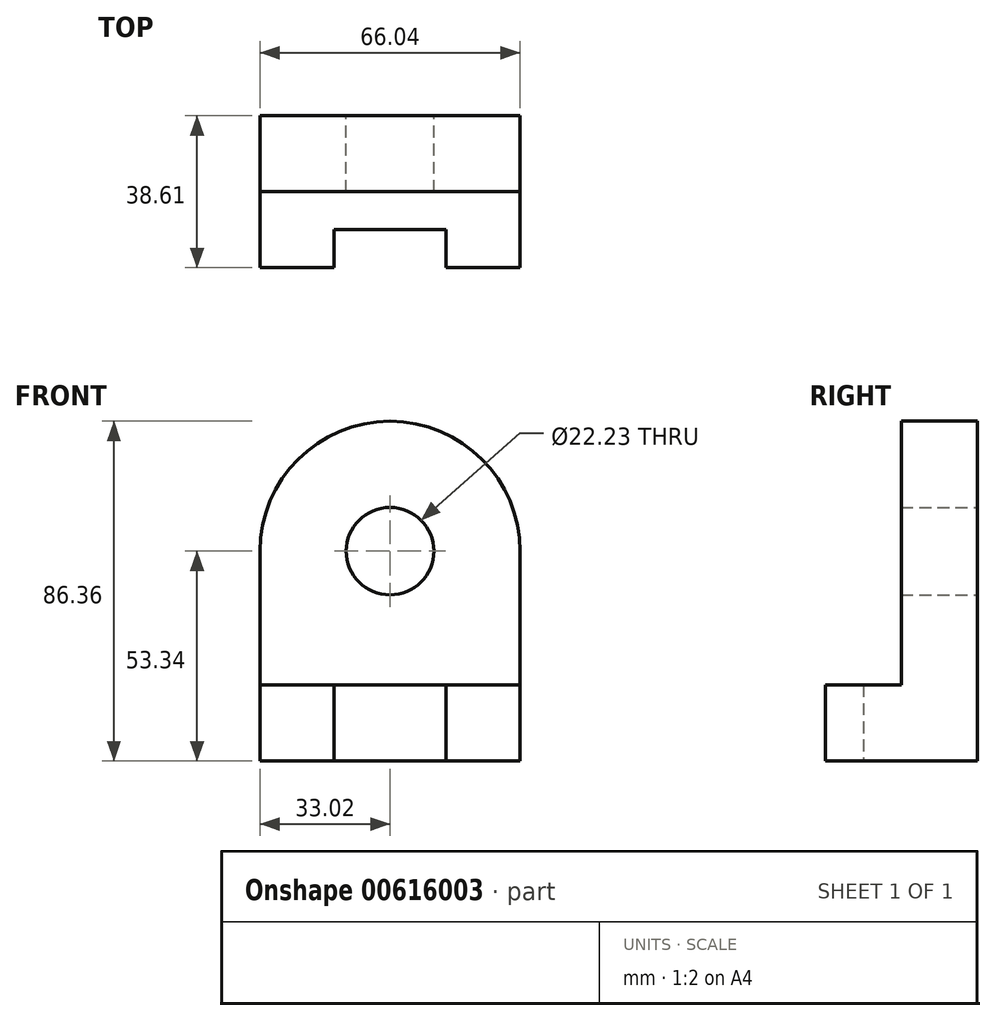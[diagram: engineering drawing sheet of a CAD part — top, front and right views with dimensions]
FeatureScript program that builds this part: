
annotation { "Feature Type Name" : "Feature", "Feature Type Description" : "" }
export const myFeature = defineFeature(function(context is Context, id is Id, definition is map)
    precondition{}
    {
        {
            var Q0;
            Q0=qCreatedBy(makeId("Front.planeOp"),FACE);
            var sketch = newSketch(context, id + "F0", { "sketchPlane" : qUnion([Q0])});
            skLineSegment(sketch, "E0.bottom", {"start": v(0, 0) * mm, "end": v(-66.04, 0) * mm});
            skLineSegment(sketch, "E0.left", {"start": v(0, 0) * mm, "end": v(0, 53.34) * mm});
            skLineSegment(sketch, "E0.right", {"start": v(-66.04, 0) * mm, "end": v(-66.04, 53.34) * mm});
            skArc(sketch, "E1", {"start": v(0, 53.34) * mm, "mid": v(-33.02, 86.36) * mm, "end": v(-66.04, 53.34) * mm});
            skCircle(sketch, "E2", {"center": v(-33.02, 53.34) * mm, "radius": 11.11 * mm});
            skPoint(sketch, "E3", {"position": v(-66.04, 0) * mm});
            skPoint(sketch, "E4", {"position": v(0, 0) * mm});
            skSolve(sketch);
        }
        {
            var Q0;
            Q0=makeQuery(id+"F0.imprint","IMPRINT",FACE,{"disambiguationData":[TD([[makeQuery(id+"F0.imprint","IMPRINT",EDGE,{"derivedFrom":sQuery(id+"F0.wireOp",EDGE,"E0.bottom")}),-1.0]])]});
            extrude(context, id + "F1", {"entities" : qUnion([Q0]), "depth" : 19.3 * mm, "offsetDistance" : 25.4 * mm});
        }
        {
            var Q0;
            Q0=qCreatedBy(makeId("Top.planeOp"),FACE);
            var sketch = newSketch(context, id + "F2", { "sketchPlane" : qUnion([Q0])});
            skLineSegment(sketch, "E5", {"start": v(0, 0) * mm, "end": v(-66.04, 0) * mm});
            skLineSegment(sketch, "E6", {"start": v(-66.04, 0) * mm, "end": v(-66.04, -38.6) * mm});
            skLineSegment(sketch, "E7", {"start": v(-66.04, -38.6) * mm, "end": v(-47.24, -38.6) * mm});
            skLineSegment(sketch, "E8", {"start": v(-47.24, -38.6) * mm, "end": v(-47.24, -28.96) * mm});
            skLineSegment(sketch, "E9", {"start": v(-18.8, -28.96) * mm, "end": v(-47.24, -28.96) * mm});
            skLineSegment(sketch, "E10", {"start": v(-18.8, -28.96) * mm, "end": v(-18.8, -38.6) * mm});
            skLineSegment(sketch, "E11", {"start": v(-18.8, -38.6) * mm, "end": v(0, -38.6) * mm});
            skLineSegment(sketch, "E12", {"start": v(0, -38.6) * mm, "end": v(0, 0) * mm});
            skSolve(sketch);
        }
        {
            var Q0;
            Q0=makeQuery(id+"F2.imprint","IMPRINT",FACE,{"disambiguationData":[TD([[makeQuery(id+"F2.imprint","IMPRINT",EDGE,{"derivedFrom":sQuery(id+"F2.wireOp",EDGE,"E5")}),1.0]])]});
            extrude(context, id + "F3", {"entities" : qUnion([Q0]), "operationType" : NewBodyOperationType.ADD, "depth" : 19.3 * mm, "offsetDistance" : 25.4 * mm});
        }
    });
